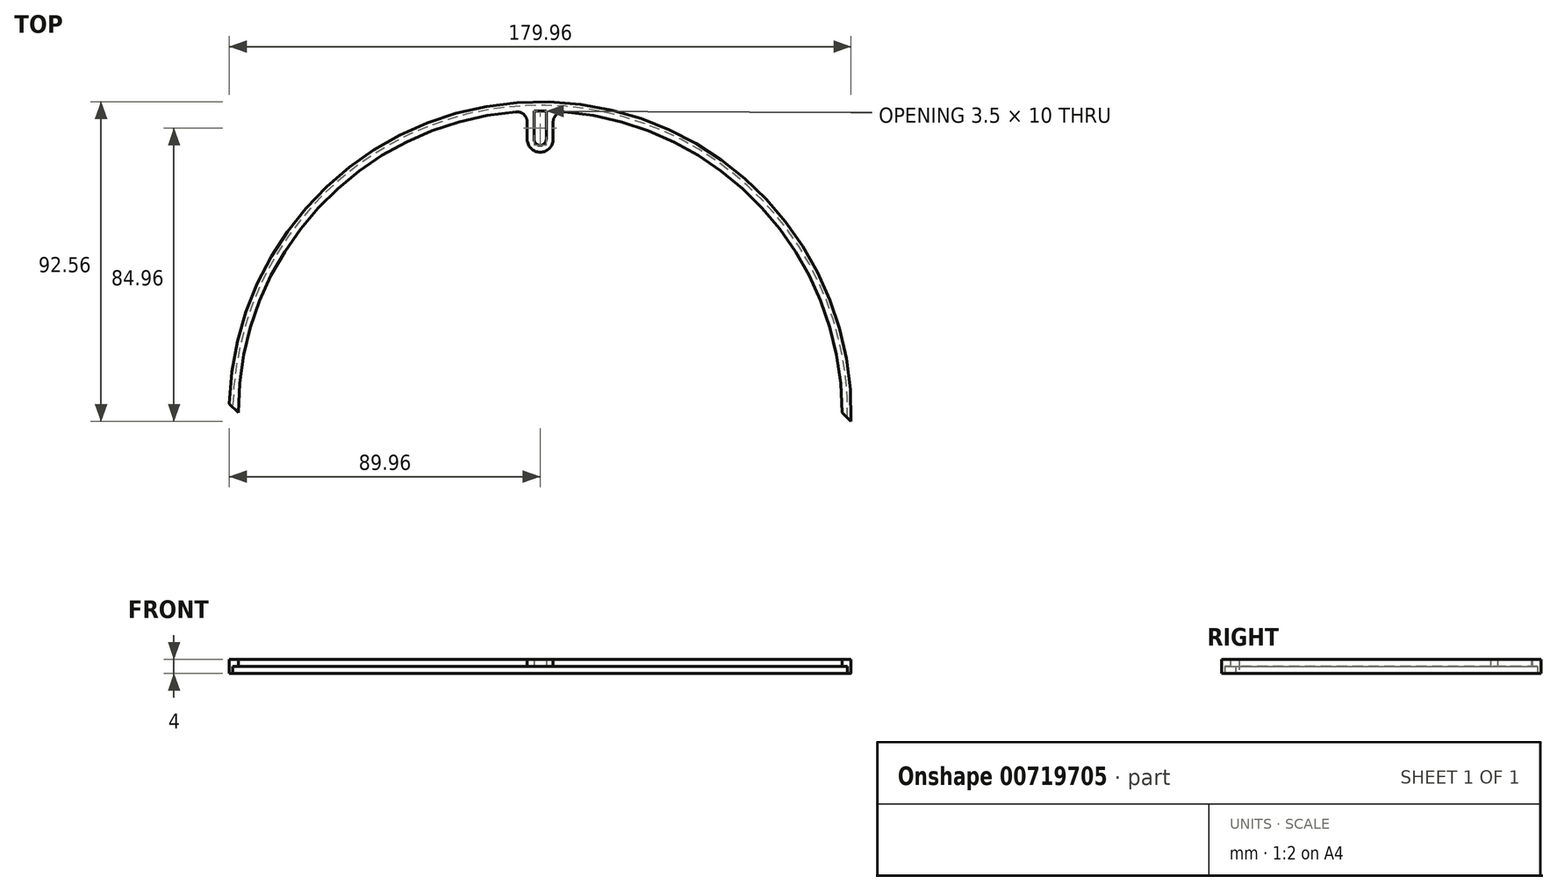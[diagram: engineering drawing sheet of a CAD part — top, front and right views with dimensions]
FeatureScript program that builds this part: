
annotation { "Feature Type Name" : "Feature", "Feature Type Description" : "" }
export const myFeature = defineFeature(function(context is Context, id is Id, definition is map)
    precondition{}
    {
        {
            var Q0;
            Q0=qCreatedBy(makeId("Top.planeOp"),FACE);
            var sketch = newSketch(context, id + "F0", { "sketchPlane" : qUnion([Q0])});
            skArc(sketch, "E0", {"start": v(89.96, -2.56) * mm, "mid": v(2.56, 89.96) * mm, "end": v(-89.96, 2.56) * mm});
            skArc(sketch, "E1", {"start": v(-6.99, 87.12) * mm, "mid": v(-64.22, 59.28) * mm, "end": v(-87.4, 0) * mm});
            skLineSegment(sketch, "E2.right", {"start": v(-3.75, 84.13) * mm, "end": v(-3.75, 79.15) * mm});
            skArc(sketch, "E3", {"start": v(-3.75, 79.15) * mm, "mid": v(0, 75.4) * mm, "end": v(3.75, 79.15) * mm});
            skLineSegment(sketch, "E4.trimOffspring", {"start": v(3.75, 84.13) * mm, "end": v(3.75, 79.15) * mm});
            skArc(sketch, "E5.trimOffspring", {"start": v(87.4, 0) * mm, "mid": v(64.22, 59.28) * mm, "end": v(6.99, 87.12) * mm});
            skArc(sketch, "E6", {"start": v(-1.75, 79.15) * mm, "mid": v(0, 77.4) * mm, "end": v(1.75, 79.15) * mm});
            skLineSegment(sketch, "E7", {"start": v(-1.75, 79.15) * mm, "end": v(-1.75, 87.4) * mm});
            skLineSegment(sketch, "E8", {"start": v(-1.75, 87.4) * mm, "end": v(1.75, 87.4) * mm});
            skLineSegment(sketch, "E9", {"start": v(1.75, 87.4) * mm, "end": v(1.75, 79.15) * mm});
            skPoint(sketch, "E10.visualSharp", {"position": v(-3.75, 87.32) * mm});
            skArc(sketch, "E10.filletArc", {"start": v(-3.75, 84.13) * mm, "mid": v(-4.72, 86.33) * mm, "end": v(-6.99, 87.12) * mm});
            skPoint(sketch, "E11.visualSharp", {"position": v(3.75, 87.32) * mm});
            skArc(sketch, "E11.filletArc", {"start": v(6.99, 87.12) * mm, "mid": v(4.72, 86.33) * mm, "end": v(3.75, 84.13) * mm});
            skLineSegment(sketch, "E12", {"start": v(-87.4, 0) * mm, "end": v(-89.96, 2.56) * mm});
            skLineSegment(sketch, "E13", {"start": v(87.4, 0) * mm, "end": v(89.96, -2.56) * mm});
            skSolve(sketch);
        }
        {
            var Q0;
            Q0 = qSketchRegion(id + "F0", true);
            extrude(context, id + "F1", {"entities" : qUnion([Q0]), "depth" : 4 * mm, "offsetDistance" : 25 * mm});
        }
        {
            var Q0;
            Q0=qCreatedBy(makeId("Top.planeOp"),FACE);
            var sketch = newSketch(context, id + "F2", { "sketchPlane" : qUnion([Q0])});
            skCircle(sketch, "E14", {"center": v(0, 0) * mm, "radius": 89 * mm});
            skLineSegment(sketch, "E15", {"start": v(0, 0) * mm, "end": v(-77.08, 44.5) * mm, "construction": true});
            skLineSegment(sketch, "E16", {"start": v(-77.08, 44.5) * mm, "end": v(77.08, 44.5) * mm, "construction": true});
            skLineSegment(sketch, "E17", {"start": v(77.08, 44.5) * mm, "end": v(0, 0) * mm, "construction": true});
            skCircle(sketch, "E18", {"center": v(0, 0) * mm, "radius": 87.4 * mm, "construction": true});
            skSolve(sketch);
        }
        {
            var Q0;
            Q0 = qSketchRegion(id + "F2", true);
            extrude(context, id + "F3", {"entities" : qUnion([Q0]), "operationType" : NewBodyOperationType.REMOVE, "depth" : 2 * mm, "offsetDistance" : 25 * mm});
        }
    });
